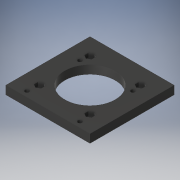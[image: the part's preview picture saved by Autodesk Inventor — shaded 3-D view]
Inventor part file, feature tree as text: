
AUTODESK INVENTOR PART (.ipt)
format: ipt  version: 2017 (Build 210142000, 142)  size: 231,936 bytes
history: native  units: in
note: dims shown in document units (in); Inventor stores cm internally (conversion verified against a paired STEP export)
features: extrude x5, sketch x5, projected_geometry x2
ambient origin geometry x8: Origin, YZ Plane, XZ Plane, XY Plane, X Axis, Y Axis, Z Axis, Center Point
bodies: Solid1 (feature_tree)
feature tree (12):
  extrude  "Extrusion1"  Depth=2.5in
  extrude  "Extrusion2"  TaperAngle=180.0deg  [1 undecoded]
  extrude  "Extrusion3"  Depth=0.125in
  extrude  "Extrusion4"  Depth=0.125in TaperAngle=0.0deg
  extrude  "Extrusion5"  Depth=1.5in
  sketch  "Sketch1"  dims[d0=2.5in d1=2.5in]
  sketch  "Sketch2"  dims[d2=0.75in d3=180.0deg]
  projected_geometry  "Projected Loop1"
  sketch  "Sketch5"  dims[d6=0.7874in d8=1.5in d9=0.7874in d11=1.5in d14=0.125in d15=0.0in]
  sketch  "Sketch6"  dims[d16=0.25in d17=0.7874in d19=1.5in d20=0.7874in d22=1.5in d25=0.125in d26=0.0in d41=0.7875in d42=0.95in d43=0.125in d44=1.575in d45=1.575in d46=0.1875in d49=0.125in d50=0.0in d51=0.1875in d52=0.1875in d53=0.1875in d54=0.1875in d55=0.125in d56=0.0in d57=0.125in d58=0.0in]
  projected_geometry  "Projected Loop3"
  sketch  "Sketch4"  dims[d4=0.75in d5=0.125in]
note: 1 required parameter value undecoded (feature->parameter linkage not recoverable at this tier; creation-order binding heuristic only, values carry confidence <= 0.55)
